# Revit family: MJC Framing Timber
name_source: partatom
category: Structural Framing
revit_build: Autodesk Revit 2014 (Build: 20130308_1515(x64)
units: mm (PartAtom-declared; Revit-internal decimal feet)

## types (8) — shared parameters
Nog line on = Yes
Shape = Rectangle
zero-valued in all types: W

## per-type parameters (varying)
| type | A | b | d |
| 190 x 45 | 0.01 m² | 45 mm  [stored 0.147638 ft] | 190 mm |
| 140 x 90 Brace | 0.01 m² | 90 mm  [stored 0.295276 ft] | 140 mm  [stored 0.459318 ft] |
| 140x45 | 0.01 m² | 45 mm  [stored 0.147638 ft] | 140 mm  [stored 0.459318 ft] |
| 90x45 | 0 m² | 45 mm  [stored 0.147638 ft] | 90 mm  [stored 0.295276 ft] |
| 290 x 45 | 0.01 m² | 45 mm  [stored 0.147638 ft] | 290 mm  [stored 0.951444 ft] |
| 247 x 47 | 0.01 m² | 47 mm  [stored 0.154199 ft] | 247 mm |
| 45x90 | 0 m² | 90 mm  [stored 0.295276 ft] | 45 mm  [stored 0.147638 ft] |
| 240 x 45 | 0.01 m² | 45 mm  [stored 0.147638 ft] | 240 mm  [stored 0.787402 ft] |

note: [stored X ft] marks values corroborated as IEEE doubles in the binary element streams (Revit-internal decimal feet)

## geometry (parser evidence)
native form markers: Sweep x1
no freeform markers — native parametric forms only
